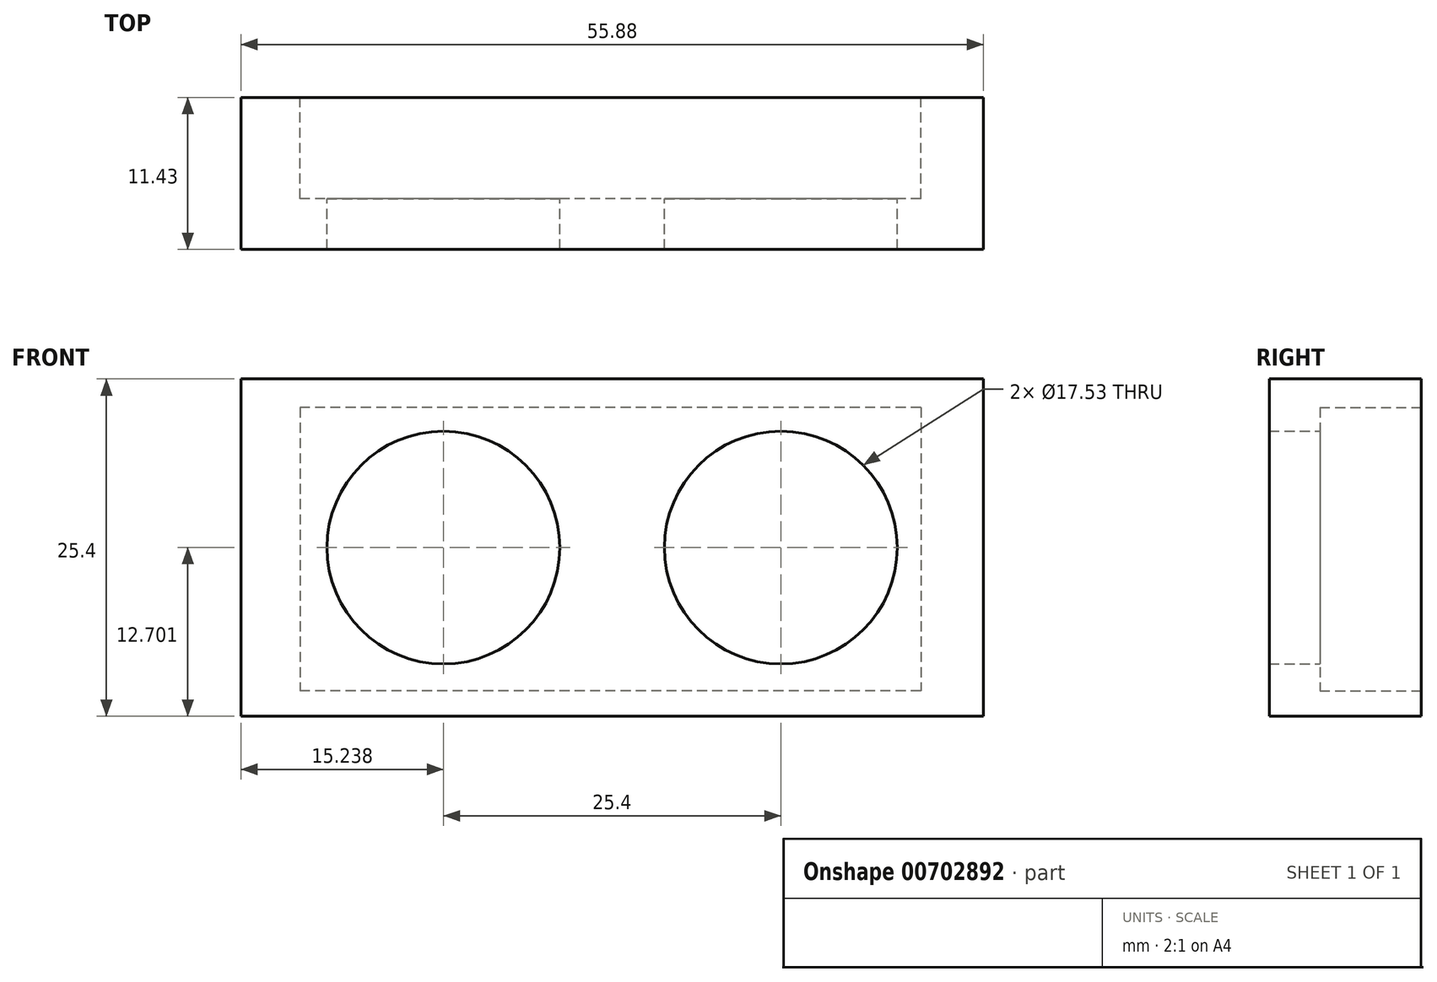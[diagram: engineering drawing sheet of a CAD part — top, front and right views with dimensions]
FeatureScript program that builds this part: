
annotation { "Feature Type Name" : "Feature", "Feature Type Description" : "" }
export const myFeature = defineFeature(function(context is Context, id is Id, definition is map)
    precondition{}
    {
        {
            var Q0;
            Q0=qCreatedBy(makeId("Front.planeOp"),FACE);
            var sketch = newSketch(context, id + "F0", { "sketchPlane" : qUnion([Q0])});
            skLineSegment(sketch, "E0.bottom", {"start": v(-34.92, 17) * mm, "end": v(20.96, 17) * mm});
            skLineSegment(sketch, "E0.top", {"start": v(-34.92, -8.4) * mm, "end": v(20.96, -8.4) * mm});
            skLineSegment(sketch, "E0.left", {"start": v(-34.92, 17) * mm, "end": v(-34.92, -8.4) * mm});
            skLineSegment(sketch, "E0.right", {"start": v(20.96, 17) * mm, "end": v(20.96, -8.4) * mm});
            skSolve(sketch);
        }
        {
            var Q0;
            Q0=makeQuery(id+"F0.imprint","IMPRINT",FACE,{"disambiguationData":[TD([[makeQuery(id+"F0.imprint","IMPRINT",EDGE,{"derivedFrom":sQuery(id+"F0.wireOp",EDGE,"E0.bottom")}),-1.0]])]});
            extrude(context, id + "F1", {"entities" : qUnion([Q0]), "depth" : 11.43 * mm, "offsetDistance" : 25.4 * mm});
        }
        {
            var Q0;
            Q0=makeQuery(id+"F1.opExtrude","CAP_FACE",FACE,{"disambiguationData":[OSD([sQuery(id+"F0.wireOp",EDGE,"E0.bottom"),sQuery(id+"F0.wireOp",EDGE,"E0.top"),sQuery(id+"F0.wireOp",EDGE,"E0.left"),sQuery(id+"F0.wireOp",EDGE,"E0.right")])],"isStart":true});
            var sketch = newSketch(context, id + "F2", { "sketchPlane" : qUnion([Q0])});
            skCircle(sketch, "E1", {"center": v(19.68, 4.3) * mm, "radius": 8.76 * mm});
            skLineSegment(sketch, "E2", {"start": v(6.98, 17) * mm, "end": v(6.98, -8.4) * mm});
            skCircle(sketch, "E3.MirrorC", {"center": v(-5.72, 4.3) * mm, "radius": 8.76 * mm});
            skSolve(sketch);
        }
        {
            var Q0;
            Q0 = qSketchRegion(id + "F2", true);
            extrude(context, id + "F3", {"entities" : qUnion([Q0]), "operationType" : NewBodyOperationType.REMOVE, "oppositeDirection" : true, "depth" : 25.4 * mm, "offsetDistance" : 25.4 * mm});
        }
        {
            var Q0;
            Q0=makeQuery(id+"F1.opExtrude","CAP_FACE",FACE,{"disambiguationData":[OSD([sQuery(id+"F0.wireOp",EDGE,"E0.bottom"),sQuery(id+"F0.wireOp",EDGE,"E0.top"),sQuery(id+"F0.wireOp",EDGE,"E0.left"),sQuery(id+"F0.wireOp",EDGE,"E0.right")])],"isStart":true});
            var sketch = newSketch(context, id + "F4", { "sketchPlane" : qUnion([Q0])});
            skLineSegment(sketch, "E4.bottom", {"start": v(-16.26, 14.83) * mm, "end": v(30.48, 14.83) * mm});
            skLineSegment(sketch, "E4.top", {"start": v(-16.26, -6.5) * mm, "end": v(30.48, -6.5) * mm});
            skLineSegment(sketch, "E4.left", {"start": v(-16.26, 14.83) * mm, "end": v(-16.26, -6.5) * mm});
            skLineSegment(sketch, "E4.right", {"start": v(30.48, 14.83) * mm, "end": v(30.48, -6.5) * mm});
            skSolve(sketch);
        }
        {
            var Q0;
            Q0=makeQuery(id+"F4.imprint","IMPRINT",FACE,{"disambiguationData":[TD([[makeQuery(id+"F4.imprint","IMPRINT",EDGE,{"derivedFrom":sQuery(id+"F4.wireOp",EDGE,"E4.bottom")}),-1.0]])]});
            extrude(context, id + "F5", {"entities" : qUnion([Q0]), "operationType" : NewBodyOperationType.REMOVE, "oppositeDirection" : true, "depth" : 7.62 * mm, "offsetDistance" : 25.4 * mm});
        }
    });
